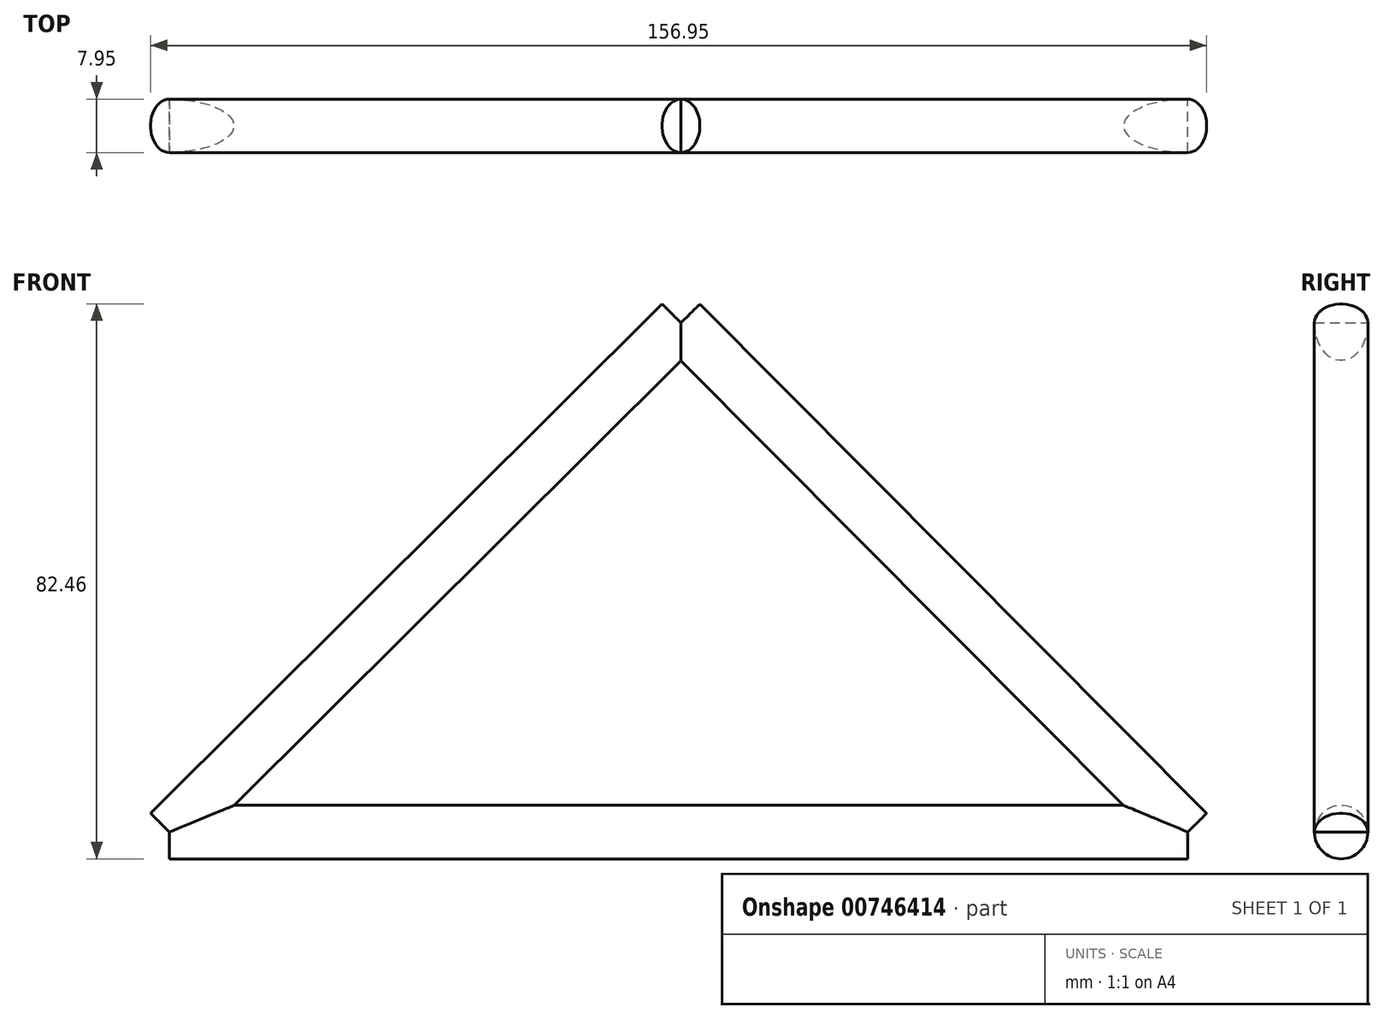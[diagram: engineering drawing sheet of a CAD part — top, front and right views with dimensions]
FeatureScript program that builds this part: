
annotation { "Feature Type Name" : "Feature", "Feature Type Description" : "" }
export const myFeature = defineFeature(function(context is Context, id is Id, definition is map)
    precondition{}
    {
        {
            var Q0;
            Q0=qCreatedBy(makeId("Front.planeOp"),FACE);
            var sketch = newSketch(context, id + "F0", { "sketchPlane" : qUnion([Q0])});
            skLineSegment(sketch, "E0", {"start": v(-76.01, 0) * mm, "end": v(0, 75.66) * mm});
            skLineSegment(sketch, "E1", {"start": v(0, 75.66) * mm, "end": v(75.31, 0) * mm});
            skLineSegment(sketch, "E2", {"start": v(75.31, 0) * mm, "end": v(-76.01, 0) * mm});
            skSolve(sketch);
        }
        {
            var Q0;
            Q0=sQuery(id+"F0.wireOp",EDGE,"E0");
            var Q1;
            Q1=sQuery(id+"F0.wireOp",EDGE,"E1");
            var Q2;
            Q2=sQuery(id+"F0.wireOp",EDGE,"E2");
            extrude(context, id + "F1", {"bodyType" : ToolBodyType.SURFACE, "surfaceEntities" : qUnion([Q0, Q1, Q2]), "depth" : 3.98 * mm, "offsetDistance" : 25.4 * mm});
        }
        {
            var Q0;
            Q0=makeQuery(id+"F1.opExtrude","SWEPT_FACE",FACE,{"disambiguationData":[OSD([sQuery(id+"F0.wireOp",EDGE,"E0")])]});
            var Q1;
            Q1=makeQuery(id+"F1.opExtrude","CAP_EDGE",EDGE,{"disambiguationData":[OSD([sQuery(id+"F0.wireOp",EDGE,"E0")])],"isStart":false});
            revolve(context, id + "F2", {"surfaceOperationType" : NewSurfaceOperationType.NEW, "entities" : qUnion([Q0]), "axis" : qUnion([Q1]), "revolveType" : RevolveType.FULL});
        }
        {
            var Q0;
            Q0=makeQuery(id+"F1.opExtrude","SWEPT_FACE",FACE,{"disambiguationData":[OSD([sQuery(id+"F0.wireOp",EDGE,"E1")])]});
            var Q1;
            Q1=makeQuery(id+"F1.opExtrude","CAP_EDGE",EDGE,{"disambiguationData":[OSD([sQuery(id+"F0.wireOp",EDGE,"E1")])],"isStart":false});
            revolve(context, id + "F3", {"operationType" : NewBodyOperationType.ADD, "surfaceOperationType" : NewSurfaceOperationType.NEW, "entities" : qUnion([Q0]), "axis" : qUnion([Q1]), "revolveType" : RevolveType.FULL});
        }
        {
            var Q0;
            Q0=makeQuery(id+"F1.opExtrude","SWEPT_FACE",FACE,{"disambiguationData":[OSD([sQuery(id+"F0.wireOp",EDGE,"E2")])]});
            var Q1;
            Q1=makeQuery(id+"F1.opExtrude","CAP_EDGE",EDGE,{"disambiguationData":[OSD([sQuery(id+"F0.wireOp",EDGE,"E2")])],"isStart":false});
            revolve(context, id + "F4", {"operationType" : NewBodyOperationType.ADD, "surfaceOperationType" : NewSurfaceOperationType.NEW, "entities" : qUnion([Q0]), "axis" : qUnion([Q1]), "revolveType" : RevolveType.FULL});
        }
    });
